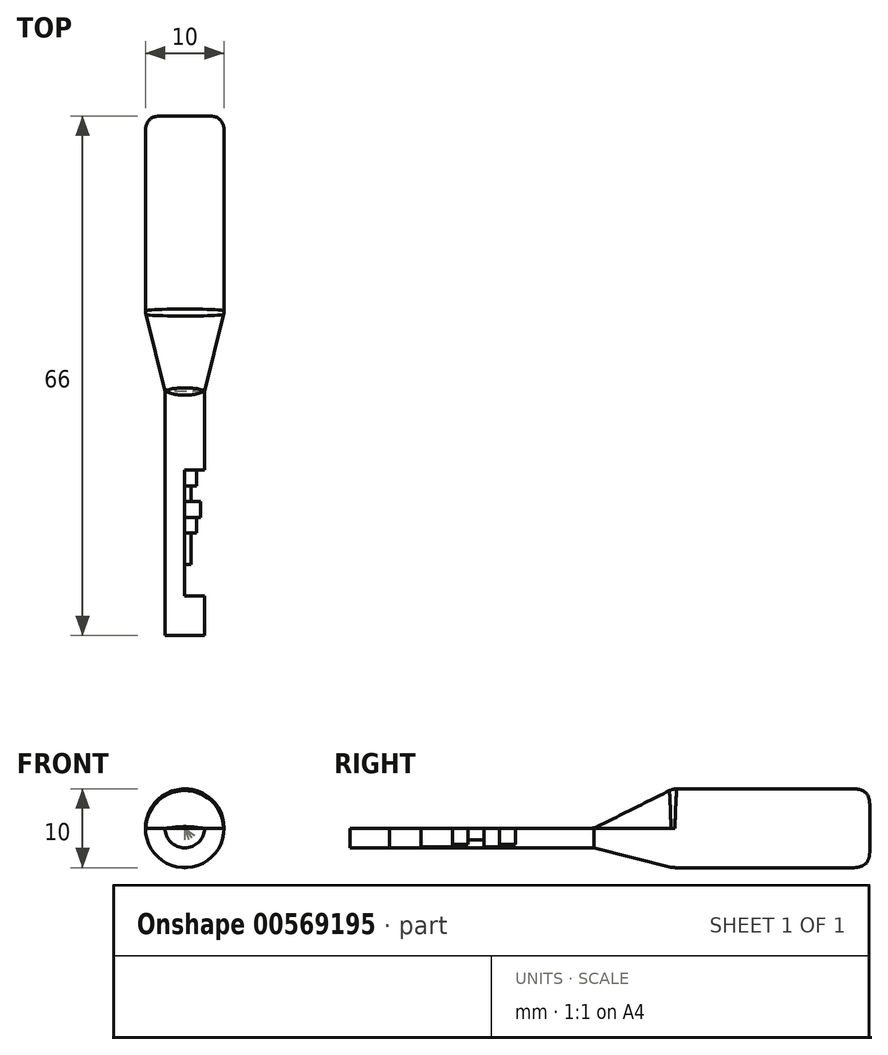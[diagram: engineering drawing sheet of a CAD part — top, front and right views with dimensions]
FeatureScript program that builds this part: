
annotation { "Feature Type Name" : "Feature", "Feature Type Description" : "" }
export const myFeature = defineFeature(function(context is Context, id is Id, definition is map)
    precondition{}
    {
        {
            var Q0;
            Q0=qCreatedBy(makeId("Front.planeOp"),FACE);
            var sketch = newSketch(context, id + "F0", { "sketchPlane" : qUnion([Q0])});
            skArc(sketch, "E0", {"start": v(-28.4, 0) * mm, "mid": v(-25.9, -2.5) * mm, "end": v(-23.4, 0) * mm});
            skLineSegment(sketch, "E1", {"start": v(-28.4, 0) * mm, "end": v(-23.4, 0) * mm});
            skSolve(sketch);
        }
        {
            var Q0;
            Q0=makeQuery(id+"F0.imprint","IMPRINT",FACE,{"disambiguationData":[TD([[makeQuery(id+"F0.imprint","IMPRINT",EDGE,{"derivedFrom":sQuery(id+"F0.wireOp",EDGE,"E0")}),1.0]])]});
            extrude(context, id + "F1", {"entities" : qUnion([Q0]), "oppositeDirection" : true, "depth" : 5 * mm, "offsetDistance" : 25 * mm});
        }
        {
            var Q0;
            Q0=makeQuery(id+"F1.opExtrude","CAP_FACE",FACE,{"disambiguationData":[OSD([sQuery(id+"F0.wireOp",EDGE,"E0"),sQuery(id+"F0.wireOp",EDGE,"E1")])],"isStart":false});
            var sketch = newSketch(context, id + "F2", { "sketchPlane" : qUnion([Q0])});
            skArc(sketch, "E2", {"start": v(25.9, -2.5) * mm, "mid": v(27.66, -1.77) * mm, "end": v(28.4, 0) * mm});
            skLineSegment(sketch, "E3", {"start": v(25.9, 0) * mm, "end": v(28.4, 0) * mm});
            skLineSegment(sketch, "E4", {"start": v(25.9, 0) * mm, "end": v(25.9, -2.5) * mm});
            skSolve(sketch);
        }
        {
            var Q0;
            Q0 = qSketchRegion(id + "F2", true);
            extrude(context, id + "F3", {"entities" : qUnion([Q0]), "operationType" : NewBodyOperationType.ADD, "depth" : 2 * mm, "offsetDistance" : 25 * mm});
        }
        {
            var Q0;
            Q0=makeQuery(id+"F3.opExtrude","CAP_FACE",FACE,{"disambiguationData":[OSD([sQuery(id+"F2.wireOp",EDGE,"E2"),sQuery(id+"F2.wireOp",EDGE,"E3"),sQuery(id+"F2.wireOp",EDGE,"E4")])],"isStart":false});
            var sketch = newSketch(context, id + "F4", { "sketchPlane" : qUnion([Q0])});
            skArc(sketch, "E5", {"start": v(25.9, -2.5) * mm, "mid": v(27.66, -1.77) * mm, "end": v(28.4, 0) * mm});
            skLineSegment(sketch, "E6", {"start": v(25.9, 0) * mm, "end": v(28.4, 0) * mm});
            skLineSegment(sketch, "E7", {"start": v(25.9, 0) * mm, "end": v(25.9, -2.5) * mm});
            skSolve(sketch);
        }
        {
            var Q0;
            Q0 = qSketchRegion(id + "F4", true);
            extrude(context, id + "F5", {"entities" : qUnion([Q0]), "operationType" : NewBodyOperationType.ADD, "depth" : 2 * mm, "offsetDistance" : 25 * mm});
        }
        {
            var Q0;
            Q0=makeQuery(id+"F5.opExtrude","CAP_FACE",FACE,{"disambiguationData":[OSD([sQuery(id+"F4.wireOp",EDGE,"E5"),sQuery(id+"F4.wireOp",EDGE,"E6"),sQuery(id+"F4.wireOp",EDGE,"E7")])],"isStart":false});
            var sketch = newSketch(context, id + "F6", { "sketchPlane" : qUnion([Q0])});
            skArc(sketch, "E8", {"start": v(25.12, -2.38) * mm, "mid": v(27.36, -2.02) * mm, "end": v(28.4, 0) * mm});
            skLineSegment(sketch, "E9", {"start": v(25.9, 0) * mm, "end": v(28.4, 0) * mm});
            skLineSegment(sketch, "E10", {"start": v(25.9, 0) * mm, "end": v(25.12, -2.38) * mm});
            skSolve(sketch);
        }
        {
            var Q0;
            Q0 = qSketchRegion(id + "F6", true);
            extrude(context, id + "F7", {"entities" : qUnion([Q0]), "operationType" : NewBodyOperationType.ADD, "depth" : 2 * mm, "offsetDistance" : 25 * mm});
        }
        {
            var Q0;
            Q0=makeQuery(id+"F7.opExtrude","CAP_FACE",FACE,{"disambiguationData":[OSD([sQuery(id+"F6.wireOp",EDGE,"E8"),sQuery(id+"F6.wireOp",EDGE,"E9"),sQuery(id+"F6.wireOp",EDGE,"E10")])],"isStart":false});
            var sketch = newSketch(context, id + "F8", { "sketchPlane" : qUnion([Q0])});
            skArc(sketch, "E11", {"start": v(25.12, -2.38) * mm, "mid": v(27.36, -2.02) * mm, "end": v(28.4, 0) * mm});
            skLineSegment(sketch, "E12", {"start": v(25.9, 0) * mm, "end": v(28.4, 0) * mm});
            skLineSegment(sketch, "E13", {"start": v(25.9, 0) * mm, "end": v(25.12, -2.38) * mm});
            skSolve(sketch);
        }
        {
            var Q0;
            Q0 = qSketchRegion(id + "F8", true);
            extrude(context, id + "F9", {"entities" : qUnion([Q0]), "operationType" : NewBodyOperationType.ADD, "depth" : 2 * mm, "offsetDistance" : 25 * mm});
        }
        {
            var Q0;
            Q0=makeQuery(id+"F9.opExtrude","CAP_FACE",FACE,{"disambiguationData":[OSD([sQuery(id+"F8.wireOp",EDGE,"E11"),sQuery(id+"F8.wireOp",EDGE,"E12"),sQuery(id+"F8.wireOp",EDGE,"E13")])],"isStart":false});
            var sketch = newSketch(context, id + "F10", { "sketchPlane" : qUnion([Q0])});
            skArc(sketch, "E14", {"start": v(24.42, -2.02) * mm, "mid": v(27.03, -2.23) * mm, "end": v(28.4, 0) * mm});
            skLineSegment(sketch, "E15", {"start": v(25.9, 0) * mm, "end": v(28.4, 0) * mm});
            skLineSegment(sketch, "E16", {"start": v(25.9, 0) * mm, "end": v(24.42, -2.02) * mm});
            skSolve(sketch);
        }
        {
            var Q0;
            Q0 = qSketchRegion(id + "F10", true);
            extrude(context, id + "F11", {"entities" : qUnion([Q0]), "operationType" : NewBodyOperationType.ADD, "depth" : 2 * mm, "offsetDistance" : 25 * mm});
        }
        {
            var Q0;
            Q0=makeQuery(id+"F11.opExtrude","CAP_FACE",FACE,{"disambiguationData":[OSD([sQuery(id+"F10.wireOp",EDGE,"E14"),sQuery(id+"F10.wireOp",EDGE,"E15"),sQuery(id+"F10.wireOp",EDGE,"E16")])],"isStart":false});
            var sketch = newSketch(context, id + "F12", { "sketchPlane" : qUnion([Q0])});
            skArc(sketch, "E17", {"start": v(23.87, -1.47) * mm, "mid": v(26.67, -2.38) * mm, "end": v(28.4, 0) * mm});
            skLineSegment(sketch, "E18", {"start": v(25.9, 0) * mm, "end": v(28.4, 0) * mm});
            skLineSegment(sketch, "E19", {"start": v(25.9, 0) * mm, "end": v(23.87, -1.47) * mm});
            skSolve(sketch);
        }
        {
            var Q0;
            Q0 = qSketchRegion(id + "F12", true);
            extrude(context, id + "F13", {"entities" : qUnion([Q0]), "operationType" : NewBodyOperationType.ADD, "depth" : 2 * mm, "offsetDistance" : 25 * mm});
        }
        {
            var Q0;
            Q0=makeQuery(id+"F13.opExtrude","CAP_FACE",FACE,{"disambiguationData":[OSD([sQuery(id+"F12.wireOp",EDGE,"E17"),sQuery(id+"F12.wireOp",EDGE,"E18"),sQuery(id+"F12.wireOp",EDGE,"E19")])],"isStart":false});
            var sketch = newSketch(context, id + "F14", { "sketchPlane" : qUnion([Q0])});
            skArc(sketch, "E20", {"start": v(25.12, -2.38) * mm, "mid": v(27.36, -2.02) * mm, "end": v(28.4, 0) * mm});
            skLineSegment(sketch, "E21", {"start": v(25.9, 0) * mm, "end": v(28.4, 0) * mm});
            skLineSegment(sketch, "E22", {"start": v(25.9, 0) * mm, "end": v(25.12, -2.38) * mm});
            skSolve(sketch);
        }
        {
            var Q0;
            Q0 = qSketchRegion(id + "F14", true);
            extrude(context, id + "F15", {"entities" : qUnion([Q0]), "operationType" : NewBodyOperationType.ADD, "depth" : 2 * mm, "offsetDistance" : 25 * mm});
        }
        {
            var Q0;
            Q0=makeQuery(id+"F15.opExtrude","CAP_FACE",FACE,{"disambiguationData":[OSD([sQuery(id+"F14.wireOp",EDGE,"E20"),sQuery(id+"F14.wireOp",EDGE,"E21"),sQuery(id+"F14.wireOp",EDGE,"E22")])],"isStart":false});
            var sketch = newSketch(context, id + "F16", { "sketchPlane" : qUnion([Q0])});
            skArc(sketch, "E23", {"start": v(24.42, -2.02) * mm, "mid": v(27.03, -2.23) * mm, "end": v(28.4, 0) * mm});
            skLineSegment(sketch, "E24", {"start": v(25.9, 0) * mm, "end": v(28.4, 0) * mm});
            skLineSegment(sketch, "E25", {"start": v(25.9, 0) * mm, "end": v(24.42, -2.02) * mm});
            skSolve(sketch);
        }
        {
            var Q0;
            Q0 = qSketchRegion(id + "F16", true);
            extrude(context, id + "F17", {"entities" : qUnion([Q0]), "operationType" : NewBodyOperationType.ADD, "depth" : 2 * mm, "offsetDistance" : 25 * mm});
        }
        {
            var Q0;
            Q0=makeQuery(id+"F17.opExtrude","CAP_FACE",FACE,{"disambiguationData":[OSD([sQuery(id+"F16.wireOp",EDGE,"E23"),sQuery(id+"F16.wireOp",EDGE,"E24"),sQuery(id+"F16.wireOp",EDGE,"E25")])],"isStart":false});
            var sketch = newSketch(context, id + "F18", { "sketchPlane" : qUnion([Q0])});
            skArc(sketch, "E26", {"start": v(23.4, 0) * mm, "mid": v(25.9, -2.5) * mm, "end": v(28.4, 0) * mm});
            skLineSegment(sketch, "E27", {"start": v(25.9, 0) * mm, "end": v(28.4, 0) * mm});
            skLineSegment(sketch, "E28", {"start": v(25.9, 0) * mm, "end": v(23.4, 0) * mm});
            skSolve(sketch);
        }
        {
            var Q0;
            Q0 = qSketchRegion(id + "F18", true);
            extrude(context, id + "F19", {"entities" : qUnion([Q0]), "operationType" : NewBodyOperationType.ADD, "depth" : 10 * mm, "offsetDistance" : 25 * mm});
        }
        {
            var Q0;
            Q0=makeQuery(id+"F19.opExtrude","CAP_FACE",FACE,{"disambiguationData":[OSD([sQuery(id+"F18.wireOp",EDGE,"E26"),sQuery(id+"F18.wireOp",EDGE,"E27"),sQuery(id+"F18.wireOp",EDGE,"E28")])],"isStart":false});
            cPlane(context, id + "F20", {"entities" : qUnion([Q0]), "cplaneType" : CPlaneType.OFFSET, "offset" : 10 * mm, "width" : 150 * mm, "height" : 150 * mm});
        }
        {
            var Q0;
            Q0=qCreatedBy(id+"F20.planeOp",FACE);
            var sketch = newSketch(context, id + "F21", { "sketchPlane" : qUnion([Q0])});
            skCircle(sketch, "E29", {"center": v(25.9, 0) * mm, "radius": 5 * mm});
            skSolve(sketch);
        }
        {
            var Q1;
            Q1=makeQuery(id+"F19.opExtrude","CAP_FACE",FACE,{"disambiguationData":[OSD([sQuery(id+"F18.wireOp",EDGE,"E26"),sQuery(id+"F18.wireOp",EDGE,"E27"),sQuery(id+"F18.wireOp",EDGE,"E28")])],"isStart":false});
            var Q2;
            Q2=makeQuery(id+"F21.imprint","IMPRINT",FACE,{"disambiguationData":[TD([[makeQuery(id+"F21.imprint","IMPRINT",EDGE,{"derivedFrom":sQuery(id+"F21.wireOp",EDGE,"E29")}),1.0]])]});
            loft(context, id + "F22", {"operationType" : NewBodyOperationType.ADD, "sheetProfilesArray" : [{ "sheetProfileEntities" : qUnion([Q1]) }, { "sheetProfileEntities" : qUnion([Q2]) }]});
        }
        {
            var Q0;
            Q0=makeQuery(id+"F22.opLoft","CAP_FACE",FACE,{"disambiguationData":[OSD([makeQuery(id+"F21.imprint","IMPRINT",FACE,{"disambiguationData":[TD([[makeQuery(id+"F21.imprint","IMPRINT",EDGE,{"derivedFrom":sQuery(id+"F21.wireOp",EDGE,"E29")}),1.0]])]})])],"isStart":true});
            extrude(context, id + "F23", {"entities" : qUnion([Q0]), "operationType" : NewBodyOperationType.ADD, "depth" : 25 * mm, "offsetDistance" : 25 * mm});
        }
        {
            var Q0;
            {var subQ0=sQuery(id+"F21.wireOp",EDGE,"E29");var subQ1=sQuery(id+"F18.wireOp",EDGE,"E27");var subQ2=sQuery(id+"F18.wireOp",EDGE,"E26");Q0=makeQuery(id+"F23.opExtrude","CAP_EDGE",EDGE,{"disambiguationData":[OSD([subQ2,subQ1,subQ0]),TDD([makeQuery(id+"F22.opLoft","MID_CAP_EDGE",EDGE,{"disambiguationData":[OSD([subQ2,subQ1,subQ0]),OD(1.0)],"capPos":1.0})])],"isStart":false});}
            var Q1;
            {var subQ0=sQuery(id+"F21.wireOp",EDGE,"E29");var subQ1=sQuery(id+"F18.wireOp",EDGE,"E27");var subQ2=sQuery(id+"F18.wireOp",EDGE,"E26");Q1=makeQuery(id+"F23.opExtrude","CAP_EDGE",EDGE,{"disambiguationData":[OSD([subQ2,subQ1,subQ0]),TDD([makeQuery(id+"F22.opLoft","MID_CAP_EDGE",EDGE,{"disambiguationData":[OSD([subQ2,subQ1,subQ0]),OD(0.0)],"capPos":1.0})])],"isStart":false});}
            var Q2;
            {var subQ0=sQuery(id+"F21.wireOp",EDGE,"E29");var subQ1=sQuery(id+"F18.wireOp",EDGE,"E27");var subQ2=sQuery(id+"F18.wireOp",EDGE,"E26");var subQ3=makeQuery(id+"F22.opLoft","MID_CAP_EDGE",EDGE,{"disambiguationData":[OSD([subQ2,subQ1,subQ0]),OD(1.0)],"capPos":1.0});Q2=makeQuery(id+"F23.boolean.opBoolean","MERGE",EDGE,{"derivedFrom":[subQ3,makeQuery(id+"F23.opExtrude","CAP_EDGE",EDGE,{"disambiguationData":[OSD([subQ2,subQ1,subQ0]),TDD([subQ3])],"isStart":true})]});}
            var Q3;
            {var subQ0=sQuery(id+"F21.wireOp",EDGE,"E29");var subQ1=sQuery(id+"F18.wireOp",EDGE,"E27");var subQ2=sQuery(id+"F18.wireOp",EDGE,"E26");var subQ3=makeQuery(id+"F22.opLoft","MID_CAP_EDGE",EDGE,{"disambiguationData":[OSD([subQ2,subQ1,subQ0]),OD(0.0)],"capPos":1.0});Q3=makeQuery(id+"F23.boolean.opBoolean","MERGE",EDGE,{"derivedFrom":[subQ3,makeQuery(id+"F23.opExtrude","CAP_EDGE",EDGE,{"disambiguationData":[OSD([subQ2,subQ1,subQ0]),TDD([subQ3])],"isStart":true})]});}
            var Q4;
            {var subQ0=sQuery(id+"F18.wireOp",EDGE,"E28");var subQ1=sQuery(id+"F18.wireOp",EDGE,"E27");var subQ2=makeQuery(id+"F19.opExtrude","CAP_EDGE",EDGE,{"disambiguationData":[OSD([subQ1,subQ0])],"isStart":false});var subQ3=sQuery(id+"F18.wireOp",EDGE,"E26");Q4=makeQuery(id+"F22.boolean.opBoolean","MERGE",EDGE,{"derivedFrom":[subQ2,makeQuery(id+"F22.opLoft","MID_CAP_EDGE",EDGE,{"disambiguationData":[OSD([subQ3,subQ1,subQ0]),TDD([makeQuery(id+"F19.opExtrude","CAP_VERTEX",VERTEX,{"disambiguationData":[OSD([subQ3,subQ1])],"isStart":false}),makeQuery(id+"F19.opExtrude","CAP_VERTEX",VERTEX,{"disambiguationData":[OSD([subQ3,subQ0])],"isStart":false}),subQ2])],"capPos":0.0})]});}
            fillet(context, id + "F24", {"entities" : qUnion([Q0, Q1, Q2, Q3, Q4]), "radius" : 2 * mm, "tangentPropagation" : true, "rho" : 0.5, "crossSection" : FilletCrossSection.CONIC, "allowEdgeOverflow" : false});
        }
    });
